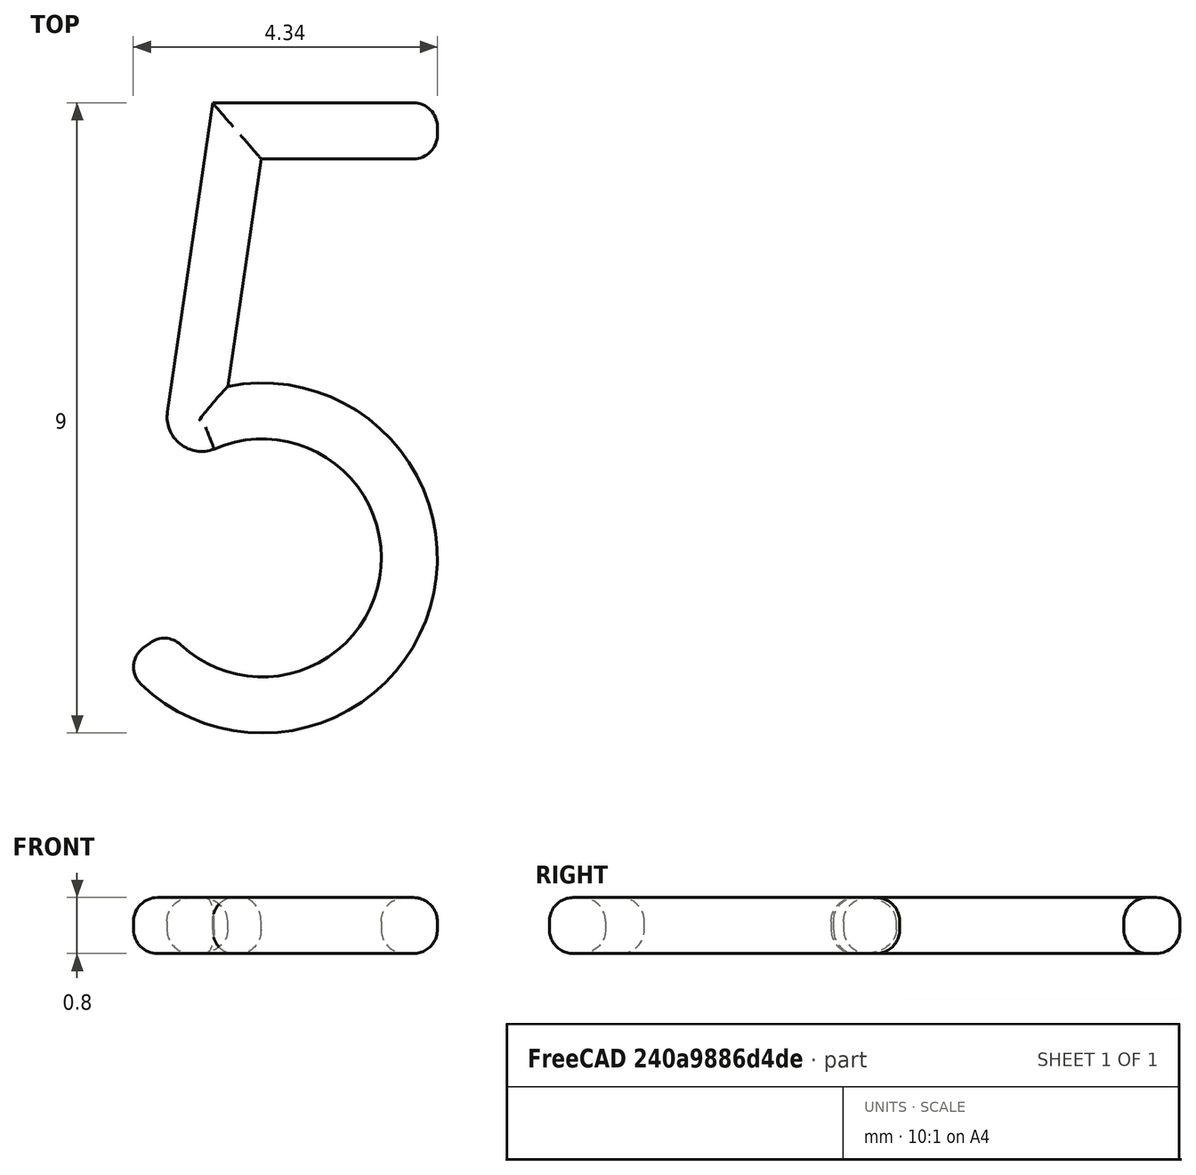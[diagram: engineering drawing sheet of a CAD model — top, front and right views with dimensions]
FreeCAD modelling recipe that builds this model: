
FCSTD DOCUMENT  (FreeCAD 0.16R6712 (Git))
Label: 5f
License: All rights reserved
LicenseURL: http://en.wikipedia.org/wiki/All_rights_reserved
objects: Sketcher::SketchObject×1, PartDesign::Pad×1, PartDesign::Fillet×1, Mesh::Feature×1
note: 4 computed .brp shape members not serialized (recipe doc carries the construction recipe); baked Part::Feature solids carry a one-line shape summary decoded from their .brp

FEATURE [Sketcher::SketchObject] Sketch
  sketch-geometry (9):
    g0: ArcOfCircle CenterX=0 CenterY=2.5 CenterZ=0 NormalX=0 NormalY=0 NormalZ=1 Radius=2.5 StartAngle=3.78977 EndAngle=8.05158
    g1: LineSegment StartX=-0.490788 StartY=4.95135 StartZ=0 EndX=-0.01651 EndY=8.2 EndZ=0
    g2: LineSegment StartX=-0.01651 StartY=8.2 StartZ=0 EndX=2.5 EndY=8.2 EndZ=0
    g3: LineSegment StartX=-0.708197 StartY=9 StartZ=0 EndX=2.5 EndY=9 EndZ=0
    g4: LineSegment StartX=-0.708197 StartY=9 StartZ=0 EndX=-1.35277 EndY=4.58488 EndZ=0
    g5: ArcOfCircle CenterX=0 CenterY=2.5 CenterZ=0 NormalX=0 NormalY=0 NormalZ=1 Radius=1.7 StartAngle=3.78977 EndAngle=8.26933
    g6: LineSegment StartX=-1.35522 StartY=1.47366 StartZ=0 EndX=-1.99297 EndY=0.990671 EndZ=0
    g7: LineSegment StartX=2.5 StartY=8.2 StartZ=0 EndX=2.5 EndY=9 EndZ=0
    g8: ArcOfCircle CenterX=-0.865661 CenterY=4.51376 CenterZ=0 NormalX=0 NormalY=0 NormalZ=1 Radius=0.492274 StartAngle=2.99662 EndAngle=5.08605
  constraints (24):
    c: PointOnObject(g0,g-2)
    c: Coincident(g1,g0)
    c: Coincident(g2,g1)
    c: Horizontal(g2)
    c: Tangent(g0,g-1)
    c: Radius(g0) = 2.5
    c: Horizontal(g3)
    c: Coincident(g4,g3)
    c: Coincident(g5,g0)
    c: Coincident(g6,g5)
    c: Coincident(g6,g0)
    c: Perpendicular(g0,g6)
    c: Distance(g5,g0) = 0.8
    c: DistanceX(g-1,g2) = 2.5
    c: Coincident(g7,g3)
    c: Perpendicular(g7,g2)
    c: Coincident(g7,g2)
    c: Coincident(g8,g4)
    c: Coincident(g8,g5)
    c: Tangent(g8,g4)
    c: DistanceY(g2,g3) = 0.8
    c: Distance(g-1,g3) = 9
    c: Parallel(g1,g4)
    c: Distance(g1,g4) = 0.8
FEATURE [PartDesign::Pad] Pad
  Length = 0.8
  Length2 = 100
  Midplane = true
  Sketch = -> Sketch
  Type = 0
FEATURE [PartDesign::Fillet] Fillet
  Base = -> Pad [Edge4,Edge7,Edge10,Edge13,Edge16,Edge19,Edge22,Edge25,Edge27,Edge11,Edge14,Edge15,Edge3,Edge6,Edge9,Edge12,Edge18,Edge21,Edge24,Edge26,Edge1,Edge2]
  Radius = 0.34
FEATURE [Mesh::Feature] Mesh  label="Fillet (Meshed)"
